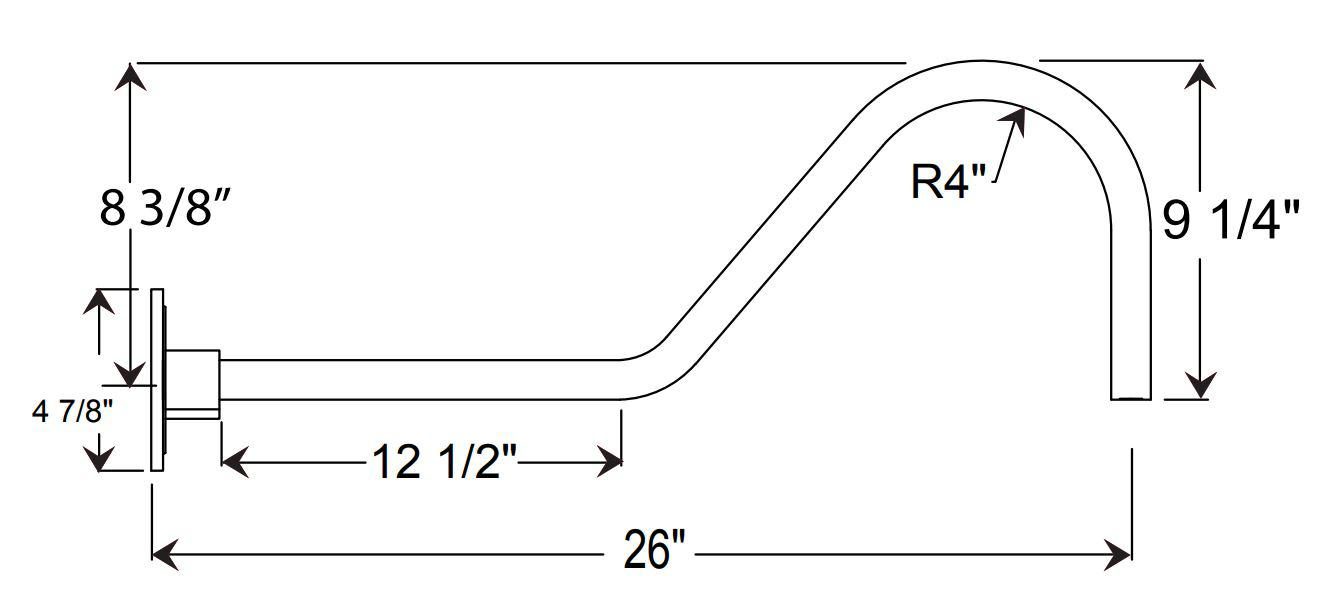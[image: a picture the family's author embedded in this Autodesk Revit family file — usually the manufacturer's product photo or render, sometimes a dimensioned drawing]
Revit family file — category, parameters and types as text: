
# Revit family: GUP110 - 6,7
name_source: partatom
category: Lighting Fixtures
units: mm (PartAtom-declared; Revit-internal decimal feet)

## family parameters
Always vertical = Yes
Cut with Voids When Loaded = No
Light Source = Yes
OmniClass Number = 23.80.70.00
OmniClass Title = Lighting
Part Type = Normal
Room Calculation Point = No
Round Connector Dimension = Use Diameter
Shared = No
Work Plane-Based = No

## types (2) — shared parameters
Apparent Load = 200 VA
Body Material = body
Color Filter = 16777215
Construction Material = Cast aluminum.
Default Elevation = 0' - 0"
Description = 120 Voltage
Dimming Lamp Color Temperature Shift = <None>
Fixture Height = 0' - 11 1/2"
Lamp = Incandescent Wire Lamp
Load Classification = Lighting
Manufacturer = ANP Lighting
Photometric Web File = generic.ies
Power Factor = 1
Tilt Angle = 90.00°
URL = https://www.anplighting.com
Voltage = 277 V
Warranty = 5 year limited warranty
Wattage Comments = 200W Max
Weight = 3.3 lbs

## per-type parameters (varying)
| type | Fixture Diameter | GUP110-6" | GUP110-7" |
| GUP110-6" | 0' - 6" | Yes | No |
| GUP110-7" | 0' - 7" | No | Yes |

note: column(s) folded — value = type name in every type: Model

## geometry (parser evidence)
native form markers: Sweep x22
no freeform markers — native parametric forms only
